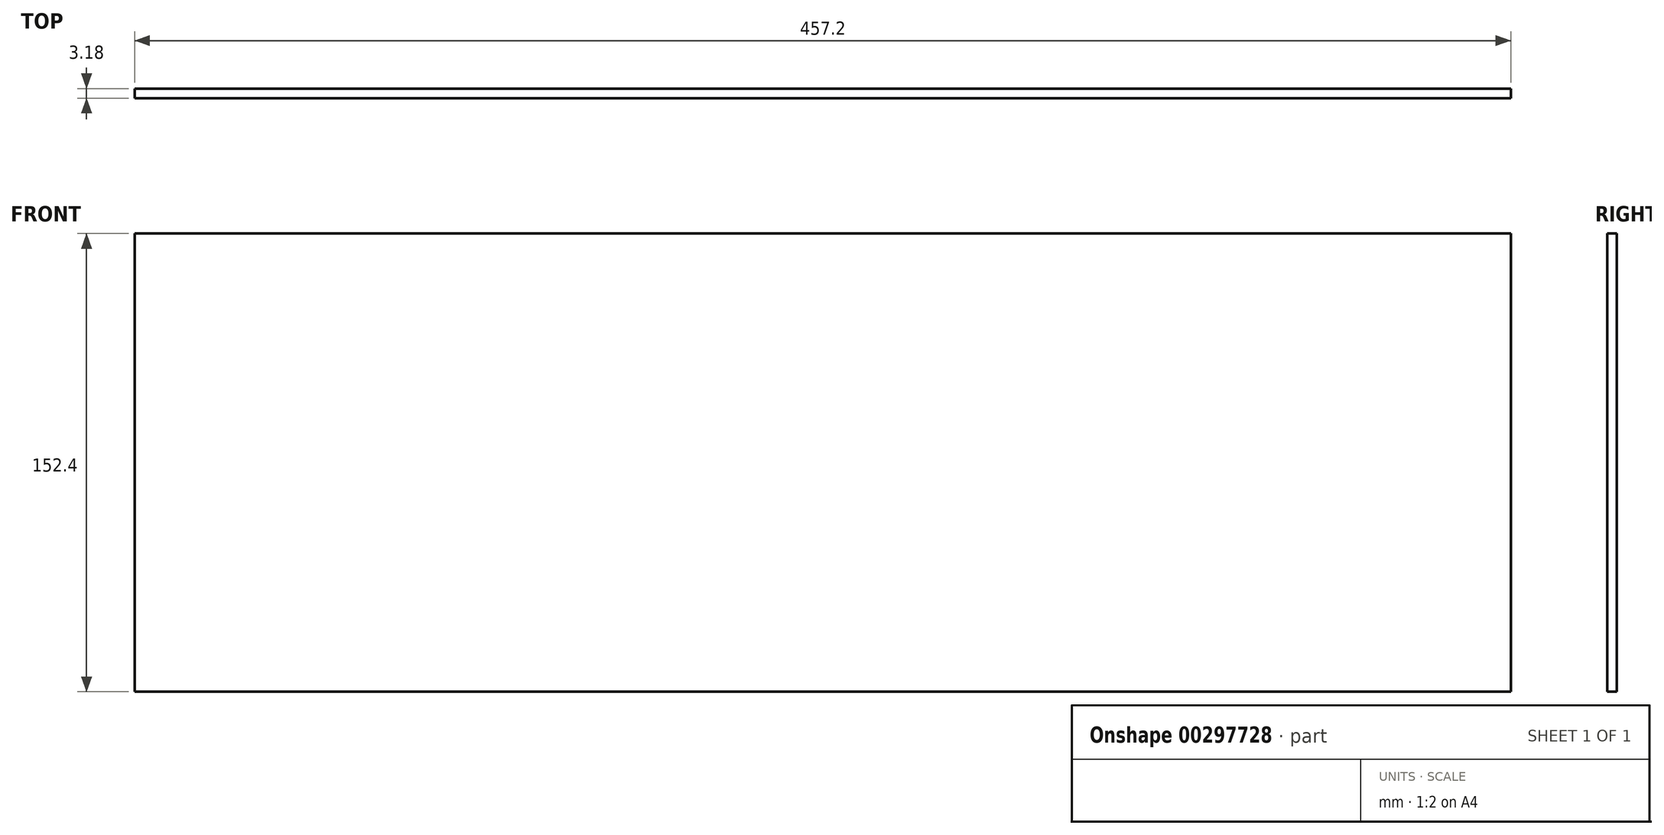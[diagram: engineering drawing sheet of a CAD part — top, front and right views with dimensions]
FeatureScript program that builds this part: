
annotation { "Feature Type Name" : "Feature", "Feature Type Description" : "" }
export const myFeature = defineFeature(function(context is Context, id is Id, definition is map)
    precondition{}
    {
        {
            var Q0;
            Q0=qCreatedBy(makeId("Front.planeOp"),FACE);
            var sketch = newSketch(context, id + "F0", { "sketchPlane" : qUnion([Q0])});
            skLineSegment(sketch, "E0.bottom", {"start": v(228.6, -76.2) * mm, "end": v(-228.6, -76.2) * mm});
            skLineSegment(sketch, "E0.top", {"start": v(228.6, 76.2) * mm, "end": v(-228.6, 76.2) * mm});
            skLineSegment(sketch, "E0.left", {"start": v(228.6, -76.2) * mm, "end": v(228.6, 76.2) * mm});
            skLineSegment(sketch, "E0.right", {"start": v(-228.6, -76.2) * mm, "end": v(-228.6, 76.2) * mm});
            skPoint(sketch, "E0.middle", {"position": v(0, 0) * mm});
            skSolve(sketch);
        }
        {
            var Q0;
            Q0 = qSketchRegion(id + "F0", true);
            extrude(context, id + "F1", {"entities" : qUnion([Q0]), "endBound" : BoundingType.SYMMETRIC, "depth" : 3.17 * mm});
        }
    });
